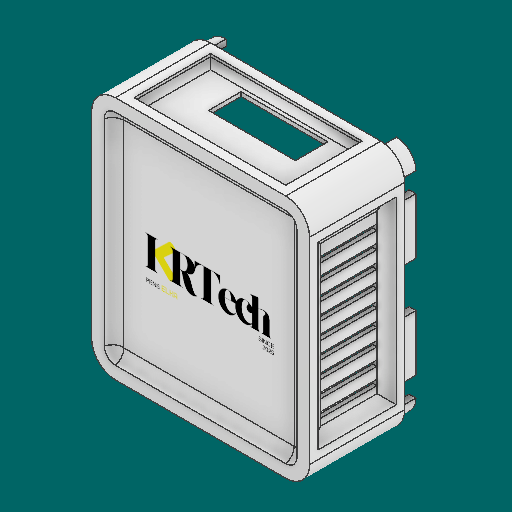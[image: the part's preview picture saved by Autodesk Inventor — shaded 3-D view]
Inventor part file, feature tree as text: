
AUTODESK INVENTOR PART (.ipt)
format: ipt  version: 2025.2 (Build 292293000, 293)  size: 673,280 bytes
history: native  units: mm
features: reference x42, sketch x14, extrude x12, other x6, fillet x3, plane x2, projected_geometry x1
ambient origin geometry x8: Origin, YZ Plane, XZ Plane, XY Plane, X Axis, Y Axis, Z Axis, Center Point
bodies: Solid1 (feature_tree)
feature tree (80):
  plane  "Work Plane1"
  extrude  "Extrusion1"  Depth=6.0mm TaperAngle=0.0deg
  extrude  "Extrusion2"  Depth=4.0mm
  extrude  "Extrusion3"  Depth=3.0mm TaperAngle=0.0deg
  fillet  "Fillet1"  Radius=4.0mm
  extrude  "Extrusion4"  Depth=3.0mm TaperAngle=0.0deg
  extrude  "Extrusion5"  Depth=2.0mm
  fillet  "Fillet2"  [1 undecoded]
  extrude  "Extrusion6"  TaperAngle=0.0deg  [1 undecoded]
  extrude  "Extrusion7"  Depth=0.2mm
  extrude  "Extrusion8"  Depth=10.0mm TaperAngle=0.0deg
  extrude  "Extrusion9"  Depth=2.0mm
  extrude  "Extrusion10"  [1 undecoded]
  extrude  "Extrusion12"  [1 undecoded]
  extrude  "Extrusion13"  [1 undecoded]
  fillet  "Fillet4"  [1 undecoded]
  plane  "Work Plane2"
  other  "Decal1"
  sketch  "Sketch1"  dims[d0=30.93mm d1=0.0mm d2=6.0mm d3=0.0mm]
  reference  "Reference1"
  sketch  "Sketch2"  dims[d7=3.0mm d8=0.0mm d9=3.0mm d10=0.0mm d11=4.0mm]
  sketch  "Sketch3"  dims[d12=3.0mm d13=0.0mm d14=3.0mm d15=0.0mm]
  sketch  "Sketch4"  dims[d17=5.6mm d18=0.0mm d19=2.0mm]
  sketch  "Sketch5"  dims[d20=10.0mm d22=10.0mm d23=280.0mm d25=2.0mm d27=0.0mm d28=0.0mm]
  sketch  "Sketch6"  dims[d29=0.25mm d30=0.0mm d31=0.0mm]
  sketch  "Sketch7"  dims[d32=0.25mm d35=0.2mm]
  sketch  "Sketch8"  dims[d36=0.2mm d37=10.0mm d38=0.0mm]
  reference  "Reference2"
  reference  "Reference3"
  reference  "Reference4"
  reference  "Reference5"
  reference  "Reference6"
  reference  "Reference7"
  reference  "Reference8"
  reference  "Reference9"
  reference  "Reference10"
  reference  "Reference11"
  reference  "Reference12"
  reference  "Reference13"
  reference  "Reference14"
  reference  "Reference15"
  reference  "Reference16"
  reference  "Reference17"
  reference  "Reference18"
  reference  "Reference19"
  reference  "Reference20"
  reference  "Reference21"
  reference  "Reference22"
  reference  "Reference23"
  reference  "Reference24"
  reference  "Reference25"
  reference  "Reference26"
  reference  "Reference27"
  reference  "Reference28"
  reference  "Reference29"
  reference  "Reference30"
  reference  "Reference31"
  reference  "Reference32"
  reference  "Reference33"
  reference  "Reference34"
  reference  "Reference35"
  sketch  "Sketch9"  dims[d39=10.0mm d40=0.0mm d41=2.0mm]
  projected_geometry  "Projected Loop1"
  sketch  "Sketch Rectangular Pattern1"  dims[d4=3.0mm d5=0.0mm d6=4.0mm]
  sketch  "Sketch10"  dims[d42=5.75mm]
  reference  "Reference36"
  reference  "Reference37"
  reference  "Reference38"
  sketch  "Sketch12"
  reference  "Reference45"
  reference  "Reference46"
  sketch  "Sketch13"
  reference  "Reference47"
  reference  "Reference48"
  sketch  "Sketch14"
  other  "Image1"
  other  "<userpath>\Downloads\cassing_hardware\Assembly1.iam"
  other  "Assembly1.iam"
  other  "part1:1"
  other  "AVR_MasImam:1"
note: 6 required parameter values undecoded (feature->parameter linkage not recoverable at this tier; creation-order binding heuristic only, values carry confidence <= 0.55)
